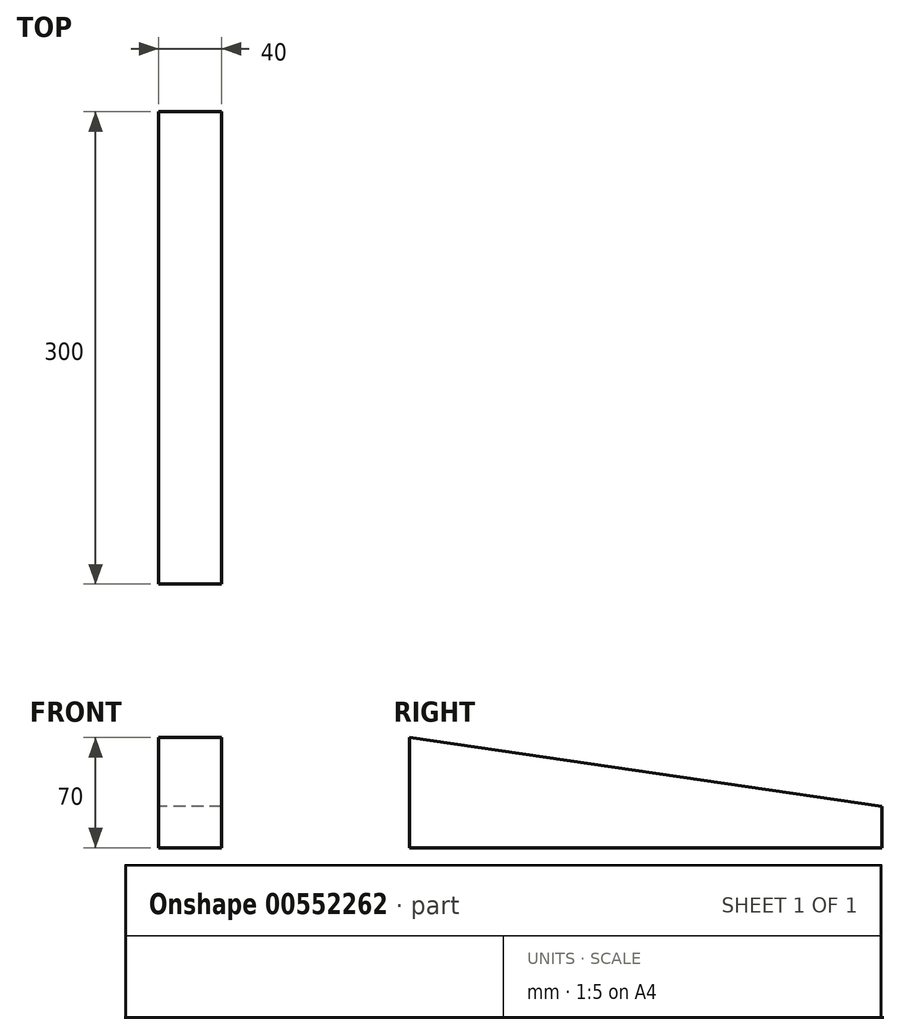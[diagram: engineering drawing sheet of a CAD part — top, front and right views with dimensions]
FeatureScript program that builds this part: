
annotation { "Feature Type Name" : "Feature", "Feature Type Description" : "" }
export const myFeature = defineFeature(function(context is Context, id is Id, definition is map)
    precondition{}
    {
        {
            var Q0;
            Q0=qCreatedBy(makeId("Right.planeOp"),FACE);
            var sketch = newSketch(context, id + "F0", { "sketchPlane" : qUnion([Q0])});
            skLineSegment(sketch, "E0.top", {"start": v(-146.83, -77.98) * mm, "end": v(153.17, -77.98) * mm});
            skLineSegment(sketch, "E0.left", {"start": v(-146.83, -7.98) * mm, "end": v(-146.83, -77.98) * mm});
            skLineSegment(sketch, "E0.right", {"start": v(153.17, -51.56) * mm, "end": v(153.17, -77.98) * mm});
            skLineSegment(sketch, "E1", {"start": v(153.17, -51.56) * mm, "end": v(-146.83, -7.98) * mm});
            skSolve(sketch);
        }
        {
            var Q0;
            Q0=makeQuery(id+"F0.imprint","IMPRINT",FACE,{"disambiguationData":[TD([[makeQuery(id+"F0.imprint","IMPRINT",EDGE,{"derivedFrom":sQuery(id+"F0.wireOp",EDGE,"E0.top")}),1.0]])]});
            extrude(context, id + "F1", {"entities" : qUnion([Q0]), "endBound" : BoundingType.SYMMETRIC, "depth" : 40 * mm, "offsetDistance" : 25 * mm});
        }
    });
